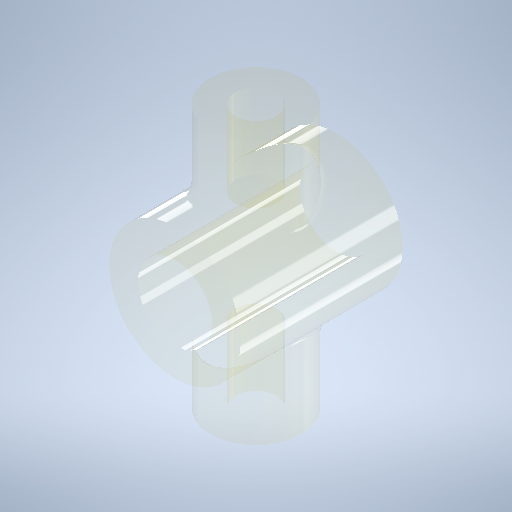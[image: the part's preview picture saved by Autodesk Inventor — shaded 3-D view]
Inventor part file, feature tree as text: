
AUTODESK INVENTOR PART (.ipt)
format: ipt  version: 2025.1 (Build 291241000, 241)  size: 375,296 bytes
history: native  units: mm
features: sketch x5, extrude x3, revolve x2, fillet x1
ambient origin geometry x8: Origin, YZ Plane, XZ Plane, XY Plane, X Axis, Y Axis, Z Axis, Center Point
bodies: Solid2 (feature_tree)
feature tree (11):
  revolve  "Revolution1"  [1 undecoded]
  revolve  "Revolution2"  [1 undecoded]
  extrude  "Extrusion8"  Depth=16.0mm
  extrude  "Extrusion9"  Depth=13.0mm
  fillet  "Congé1"  [1 undecoded]
  extrude  "Extrusion10"  Depth=14.65mm
  sketch  "Sketch8"  dims[d26=26.0mm d27=16.0mm]
  sketch  "Sketch9"  dims[d28=9.0mm d29=4.1mm]
  sketch  "Sketch10"  dims[d30=90.0deg d31=16.0mm]
  sketch  "Sketch11"  dims[d32=16.0mm d33=13.0mm d34=90.0deg d35=14.65mm d36=0.0mm d37=0.0mm d38=15.0mm d39=0.0mm d40=2.0mm d41=15.0mm d42=0.0mm]
  sketch  "Esquisse12"
note: 3 required parameter values undecoded (feature->parameter linkage not recoverable at this tier; creation-order binding heuristic only, values carry confidence <= 0.55)